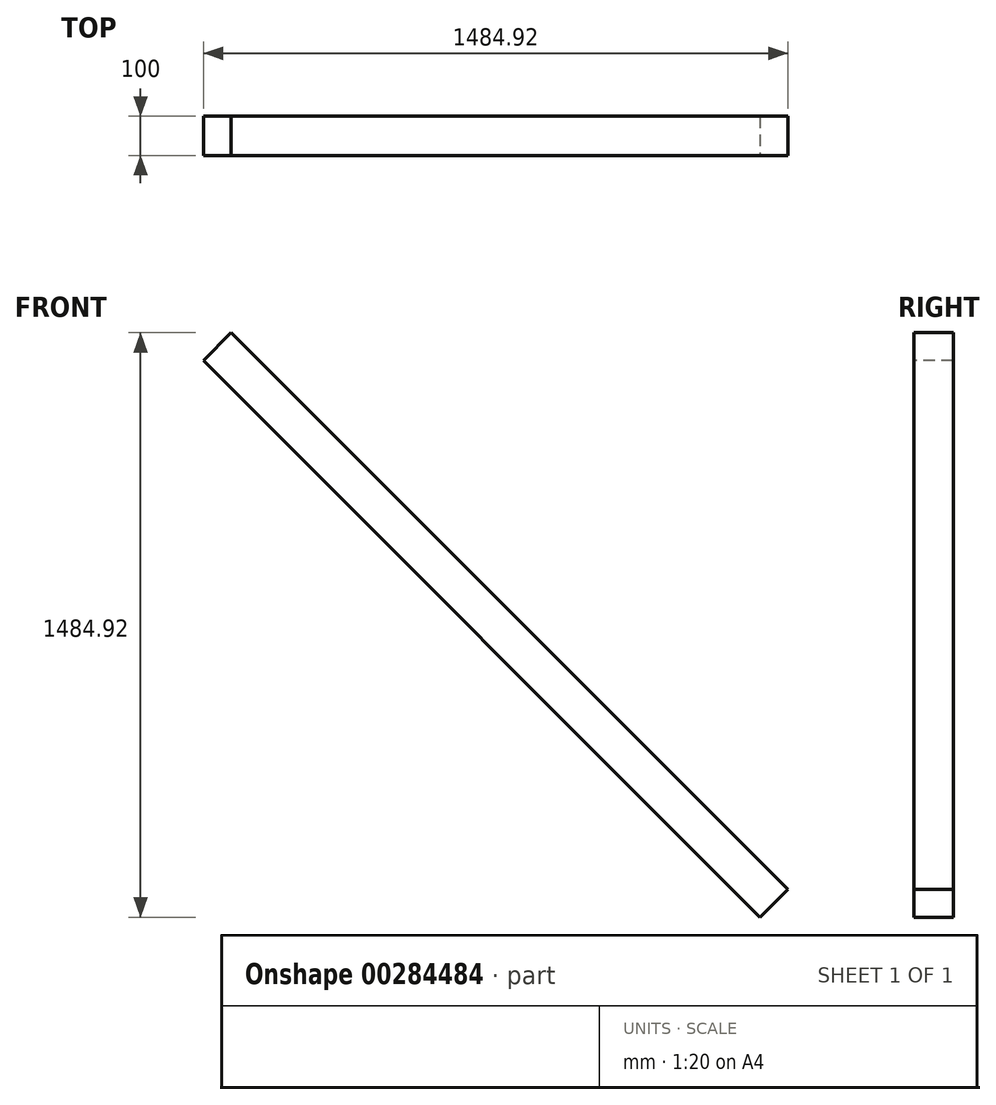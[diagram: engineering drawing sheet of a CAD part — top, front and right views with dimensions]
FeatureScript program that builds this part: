
annotation { "Feature Type Name" : "Feature", "Feature Type Description" : "" }
export const myFeature = defineFeature(function(context is Context, id is Id, definition is map)
    precondition{}
    {
        {
            var Q0;
            Q0=qCreatedBy(makeId("Right.planeOp"),FACE);
            var Q1;
            Q1=qCreatedBy(makeId("Top.planeOp"),FACE);
            cPlane(context, id + "F0", {"entities" : qUnion([Q0, Q1]), "cplaneType" : CPlaneType.MID_PLANE, "offset" : 25.4 * mm, "width" : 152.4 * mm, "height" : 152.4 * mm});
        }
        {
            var Q0;
            Q0=qCreatedBy(id+"F0.planeOp",FACE);
            var sketch = newSketch(context, id + "F1", { "sketchPlane" : qUnion([Q0])});
            skLineSegment(sketch, "E0.bottom", {"start": v(50, 50) * mm, "end": v(-50, 50) * mm});
            skLineSegment(sketch, "E0.top", {"start": v(50, -50) * mm, "end": v(-50, -50) * mm});
            skLineSegment(sketch, "E0.left", {"start": v(50, 50) * mm, "end": v(50, -50) * mm});
            skLineSegment(sketch, "E0.right", {"start": v(-50, 50) * mm, "end": v(-50, -50) * mm});
            skPoint(sketch, "E0.middle", {"position": v(0, 0) * mm});
            skSolve(sketch);
        }
        {
            var Q0;
            Q0=makeQuery(id+"F1.imprint","IMPRINT",FACE,{"disambiguationData":[TD([[makeQuery(id+"F1.imprint","IMPRINT",EDGE,{"derivedFrom":sQuery(id+"F1.wireOp",EDGE,"E0.bottom")}),1.0]])]});
            extrude(context, id + "F2", {"entities" : qUnion([Q0]), "depth" : 1000 * mm, "hasSecondDirection" : true, "secondDirectionOppositeDirection" : true, "secondDirectionDepth" : 1000 * mm});
        }
    });
